AUTODESK INVENTOR PART (.ipt)
format: ipt  version: 2022.5 (Build 265521000, 521)  size: 10,719,744 bytes
history: imported  units: in
note: dims shown in document units (in); Inventor stores cm internally (conversion verified against a paired STEP export)
features: imported_body x1
ambient origin geometry x8: Origin, YZ Plane, XZ Plane, XY Plane, X Axis, Y Axis, Z Axis, Center Point
bodies: Solid1 (imported_parasolid), Solid2 (imported_parasolid), Solid3 (imported_parasolid), Solid4 (imported_parasolid), Solid5 (imported_parasolid), Solid6 (imported_parasolid), Solid7 (imported_parasolid), Solid8 (imported_parasolid), Solid9 (imported_parasolid), Solid10 (imported_parasolid), Solid11 (imported_parasolid), Solid12 (imported_parasolid), Solid13 (imported_parasolid), Solid14 (imported_parasolid), Solid15 (imported_parasolid), Solid16 (imported_parasolid), Solid17 (imported_parasolid), Solid18 (imported_parasolid), Solid19 (imported_parasolid), Solid20 (imported_parasolid), Solid21 (imported_parasolid), Solid22 (imported_parasolid), Solid23 (imported_parasolid), Solid24 (imported_parasolid), Solid25 (imported_parasolid), Solid26 (imported_parasolid), Solid27 (imported_parasolid), Solid28 (imported_parasolid), Solid29 (imported_parasolid), Solid30 (imported_parasolid), Solid31 (imported_parasolid), Solid32 (imported_parasolid), Solid33 (imported_parasolid), Solid34 (imported_parasolid), Solid35 (imported_parasolid), Solid36 (imported_parasolid), Solid37 (imported_parasolid), Solid38 (imported_parasolid), Solid39 (imported_parasolid), Solid40 (imported_parasolid), Solid41 (imported_parasolid), Solid42 (imported_parasolid), Solid43 (imported_parasolid), Solid44 (imported_parasolid), Solid45 (imported_parasolid), Solid46 (imported_parasolid), Solid47 (imported_parasolid), Solid48 (imported_parasolid), Solid49 (imported_parasolid), Solid50 (imported_parasolid), Solid51 (imported_parasolid), Solid52 (imported_parasolid), Solid53 (imported_parasolid), Solid54 (imported_parasolid), Solid55 (imported_parasolid), Solid56 (imported_parasolid), Solid57 (imported_parasolid), Solid58 (imported_parasolid), Solid59 (imported_parasolid), Solid60 (imported_parasolid), Solid61 (imported_parasolid), Solid62 (imported_parasolid), Solid63 (imported_parasolid), Solid64 (imported_parasolid), Solid65 (imported_parasolid), Solid66 (imported_parasolid), Solid67 (imported_parasolid), Solid68 (imported_parasolid), Solid69 (imported_parasolid), Solid70 (imported_parasolid), Solid71 (imported_parasolid), Solid72 (imported_parasolid), Solid73 (imported_parasolid), Solid74 (imported_parasolid), Solid75 (imported_parasolid), Solid76 (imported_parasolid), Solid77 (imported_parasolid), Solid78 (imported_parasolid), Solid79 (imported_parasolid), Solid80 (imported_parasolid), Solid81 (imported_parasolid), Solid82 (imported_parasolid), Solid83 (imported_parasolid), Solid84 (imported_parasolid), Solid85 (imported_parasolid), Solid86 (imported_parasolid), Solid87 (imported_parasolid), Solid88 (imported_parasolid), Solid89 (imported_parasolid), Solid90 (imported_parasolid), Solid91 (imported_parasolid), Solid92 (imported_parasolid), Solid93 (imported_parasolid), Solid94 (imported_parasolid), Solid95 (imported_parasolid), Solid96 (imported_parasolid), Solid97 (imported_parasolid), Solid98 (imported_parasolid), Solid99 (imported_parasolid), Solid100 (imported_parasolid), Solid101 (imported_parasolid), Solid102 (imported_parasolid), Solid103 (imported_parasolid), Solid104 (imported_parasolid), Solid105 (imported_parasolid), Solid106 (imported_parasolid), Solid107 (imported_parasolid), Solid108 (imported_parasolid), Solid109 (imported_parasolid), Solid110 (imported_parasolid), Solid111 (imported_parasolid), Solid112 (imported_parasolid), Solid113 (imported_parasolid), Solid114 (imported_parasolid), Solid115 (imported_parasolid), Solid116 (imported_parasolid), Solid117 (imported_parasolid), Solid118 (imported_parasolid), Solid119 (imported_parasolid), Solid120 (imported_parasolid), Solid121 (imported_parasolid), Solid122 (imported_parasolid), Solid123 (imported_parasolid), Solid124 (imported_parasolid), Solid125 (imported_parasolid), Solid126 (imported_parasolid), Solid127 (imported_parasolid), Solid128 (imported_parasolid), Solid129 (imported_parasolid), Solid130 (imported_parasolid), Solid131 (imported_parasolid), Solid132 (imported_parasolid), Solid133 (imported_parasolid), Solid134 (imported_parasolid), Solid135 (imported_parasolid), Solid136 (imported_parasolid), Solid137 (imported_parasolid), Solid138 (imported_parasolid), Solid139 (imported_parasolid), Solid140 (imported_parasolid), Solid141 (imported_parasolid), Solid142 (imported_parasolid), Solid143 (imported_parasolid), Solid144 (imported_parasolid), Solid145 (imported_parasolid), Solid146 (imported_parasolid), Solid147 (imported_parasolid), Solid148 (imported_parasolid), Solid149 (imported_parasolid), Solid150 (imported_parasolid), Solid151 (imported_parasolid), Solid152 (imported_parasolid), Solid153 (imported_parasolid), Solid154 (imported_parasolid), Solid155 (imported_parasolid), Solid156 (imported_parasolid), Solid157 (imported_parasolid), Solid158 (imported_parasolid), Body1 (imported_parasolid), Body2 (imported_parasolid), Body3 (imported_parasolid), Body4 (imported_parasolid), Body5 (imported_parasolid), Body6 (imported_parasolid), Body7 (imported_parasolid), Body8 (imported_parasolid), Body9 (imported_parasolid), Body10 (imported_parasolid), Body11 (imported_parasolid), Body12 (imported_parasolid), Body13 (imported_parasolid), Body14 (imported_parasolid), Body15 (imported_parasolid), Body16 (imported_parasolid), Body17 (imported_parasolid), Body18 (imported_parasolid), Body19 (imported_parasolid), Body20 (imported_parasolid), Body21 (imported_parasolid), Body22 (imported_parasolid), Body23 (imported_parasolid), Body24 (imported_parasolid), Body25 (imported_parasolid), Body26 (imported_parasolid), Body27 (imported_parasolid), Body28 (imported_parasolid), Body29 (imported_parasolid), Body30 (imported_parasolid), Body31 (imported_parasolid), Body32 (imported_parasolid), Body33 (imported_parasolid), Body34 (imported_parasolid), Body35 (imported_parasolid), Body36 (imported_parasolid), Body37 (imported_parasolid), Body38 (imported_parasolid), Body39 (imported_parasolid), Body40 (imported_parasolid), Body41 (imported_parasolid), Body42 (imported_parasolid), Body43 (imported_parasolid), Body44 (imported_parasolid), Body45 (imported_parasolid), Body46 (imported_parasolid), Body47 (imported_parasolid), Body48 (imported_parasolid), Body49 (imported_parasolid), Body50 (imported_parasolid), Body51 (imported_parasolid), Body52 (imported_parasolid), Body53 (imported_parasolid), Body54 (imported_parasolid), Body55 (imported_parasolid), Body56 (imported_parasolid), Body57 (imported_parasolid), Body58 (imported_parasolid), Body59 (imported_parasolid), Body60 (imported_parasolid), Body61 (imported_parasolid), Body62 (imported_parasolid), Body63 (imported_parasolid), Body64 (imported_parasolid), Body65 (imported_parasolid), Body66 (imported_parasolid), Body67 (imported_parasolid), Body68 (imported_parasolid), Body69 (imported_parasolid), Body70 (imported_parasolid), Body71 (imported_parasolid), Body72 (imported_parasolid), Body73 (imported_parasolid), Body74 (imported_parasolid), Body75 (imported_parasolid), Body76 (imported_parasolid), Body77 (imported_parasolid), Body78 (imported_parasolid), Body79 (imported_parasolid), Body80 (imported_parasolid), Body81 (imported_parasolid), Body82 (imported_parasolid), Body83 (imported_parasolid), Body84 (imported_parasolid), Body85 (imported_parasolid), Body86 (imported_parasolid), Body87 (imported_parasolid), Body88 (imported_parasolid), Body89 (imported_parasolid), Body90 (imported_parasolid), Body91 (imported_parasolid), Body92 (imported_parasolid), Body93 (imported_parasolid), Body94 (imported_parasolid), Body95 (imported_parasolid), Body96 (imported_parasolid), Body97 (imported_parasolid), Body98 (imported_parasolid), Body99 (imported_parasolid), Body100 (imported_parasolid), Body101 (imported_parasolid), Body102 (imported_parasolid), Body103 (imported_parasolid), Body104 (imported_parasolid), Body105 (imported_parasolid), Body106 (imported_parasolid), Body107 (imported_parasolid), Body108 (imported_parasolid), Body109 (imported_parasolid), Body110 (imported_parasolid), Body111 (imported_parasolid), Body112 (imported_parasolid), Body113 (imported_parasolid), Body114 (imported_parasolid), Body115 (imported_parasolid), Body116 (imported_parasolid), Body117 (imported_parasolid), Body118 (imported_parasolid), Body119 (imported_parasolid), Body120 (imported_parasolid), Body121 (imported_parasolid), Body122 (imported_parasolid), Body123 (imported_parasolid), Body124 (imported_parasolid), Body125 (imported_parasolid), Body126 (imported_parasolid), Body127 (imported_parasolid), Body128 (imported_parasolid), Body129 (imported_parasolid), Body130 (imported_parasolid), Body131 (imported_parasolid), Body132 (imported_parasolid), Body133 (imported_parasolid), Body134 (imported_parasolid), Body135 (imported_parasolid), Body136 (imported_parasolid), Body137 (imported_parasolid), Body138 (imported_parasolid), Body139 (imported_parasolid), Body140 (imported_parasolid), Body141 (imported_parasolid), Body142 (imported_parasolid), Body143 (imported_parasolid), Body144 (imported_parasolid), Body145 (imported_parasolid), Body146 (imported_parasolid), Body147 (imported_parasolid), Body148 (imported_parasolid), Body149 (imported_parasolid), Body150 (imported_parasolid), Body151 (imported_parasolid), Body152 (imported_parasolid), Body153 (imported_parasolid), Body154 (imported_parasolid), Body155 (imported_parasolid), Body156 (imported_parasolid), Body157 (imported_parasolid), Body158 (imported_parasolid)
feature tree (1):
  imported_body  NMx_Import_Brep_tag  [imported B-rep: ~815 faces, bbox_mm=[39.705, 9.673596, 63.37]]
